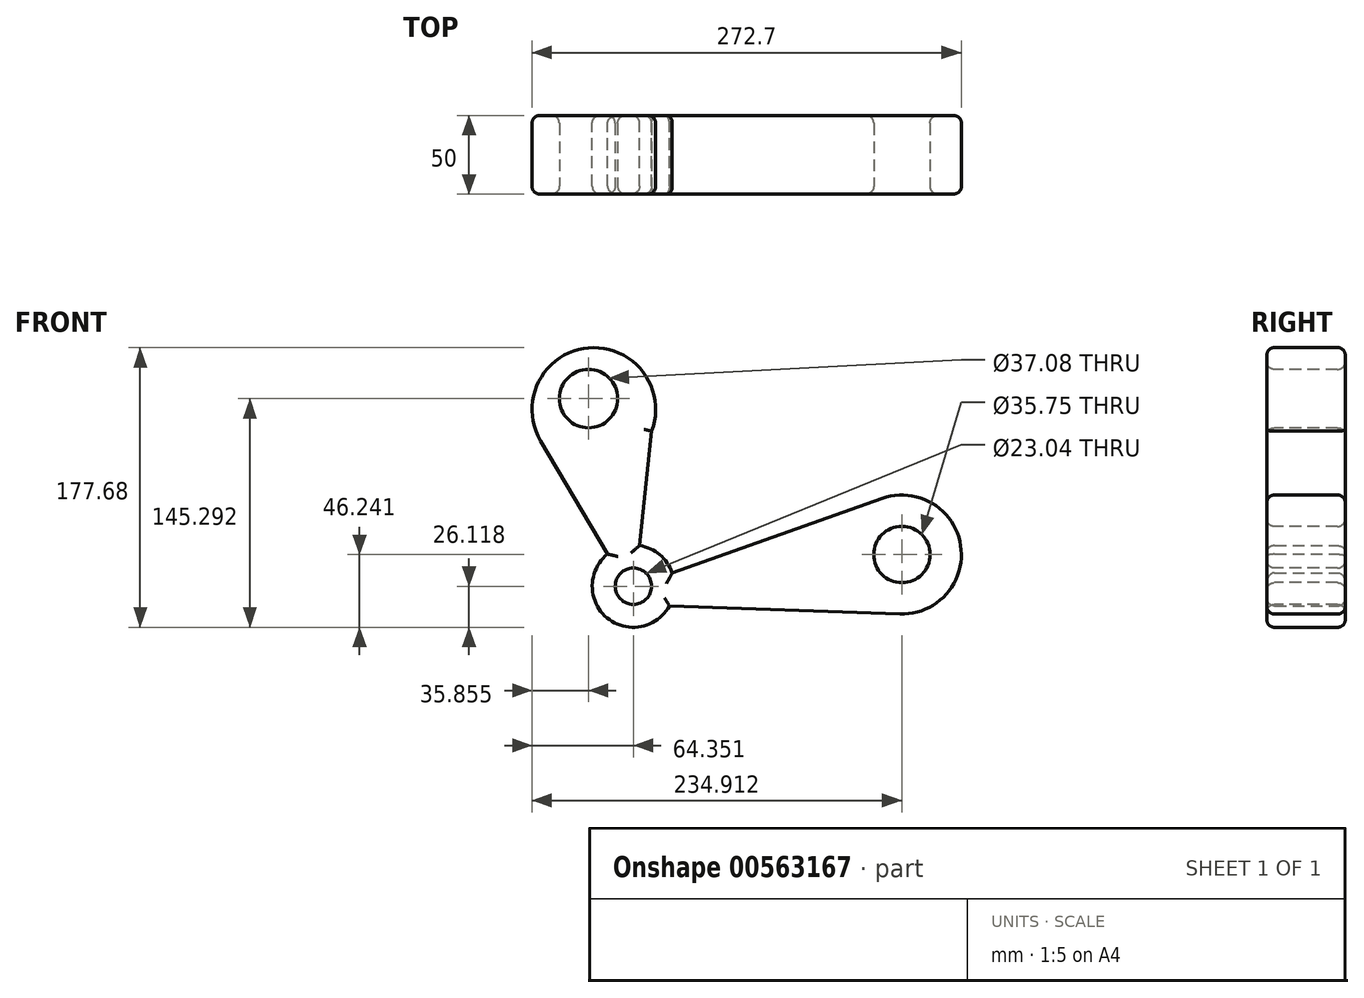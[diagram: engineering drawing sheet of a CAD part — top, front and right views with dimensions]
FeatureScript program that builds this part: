
annotation { "Feature Type Name" : "Feature", "Feature Type Description" : "" }
export const myFeature = defineFeature(function(context is Context, id is Id, definition is map)
    precondition{}
    {
        {
            var Q0;
            Q0=qCreatedBy(makeId("Front.planeOp"),FACE);
            var sketch = newSketch(context, id + "F0", { "sketchPlane" : qUnion([Q0])});
            skCircle(sketch, "E0", {"center": v(-83.68, 77.32) * mm, "radius": 39.25 * mm});
            skCircle(sketch, "E1", {"center": v(111.97, -14.86) * mm, "radius": 37.8 * mm});
            skCircle(sketch, "E2", {"center": v(-58.59, -34.98) * mm, "radius": 26.11 * mm});
            skLineSegment(sketch, "E3", {"start": v(-46.94, 63.5) * mm, "end": v(-54.54, -9.18) * mm});
            skLineSegment(sketch, "E4", {"start": v(-117.48, 57.36) * mm, "end": v(-74.96, -14.64) * mm});
            skLineSegment(sketch, "E5", {"start": v(99.34, 20.76) * mm, "end": v(-33.9, -26.48) * mm});
            skLineSegment(sketch, "E6", {"start": v(-35.66, -47.49) * mm, "end": v(110.65, -52.63) * mm});
            skSolve(sketch);
        }
        {
            var Q0;
            {var subQ0=sQuery(id+"F0.wireOp",EDGE,"E0");var subQ1=makeQuery(id+"F0.imprint","INTERSECT",VERTEX,{"derivedFrom":[subQ0,sQuery(id+"F0.wireOp",EDGE,"E3")]});Q0=makeQuery(id+"F0.imprint","IMPRINT",FACE,{"disambiguationData":[TD([[makeQuery(id+"F0.imprint","IMPRINT",EDGE,{"disambiguationData":[TD([[subQ1,1.0]])],"derivedFrom":subQ0}),1.0]])]});}
            var Q1;
            {var subQ0=sQuery(id+"F0.wireOp",EDGE,"E3");Q1=makeQuery(id+"F0.imprint","IMPRINT",FACE,{"disambiguationData":[TD([[makeQuery(id+"F0.imprint","IMPRINT",EDGE,{"derivedFrom":subQ0}),-1.0]])]});}
            var Q2;
            {var subQ0=sQuery(id+"F0.wireOp",EDGE,"E2");var subQ1=makeQuery(id+"F0.imprint","INTERSECT",VERTEX,{"derivedFrom":[subQ0,sQuery(id+"F0.wireOp",EDGE,"E3")]});Q2=makeQuery(id+"F0.imprint","IMPRINT",FACE,{"disambiguationData":[TD([[makeQuery(id+"F0.imprint","IMPRINT",EDGE,{"disambiguationData":[TD([[subQ1,1.0]])],"derivedFrom":subQ0}),1.0]])]});}
            var Q3;
            {var subQ0=sQuery(id+"F0.wireOp",EDGE,"E5");Q3=makeQuery(id+"F0.imprint","IMPRINT",FACE,{"disambiguationData":[TD([[makeQuery(id+"F0.imprint","IMPRINT",EDGE,{"derivedFrom":subQ0}),1.0]])]});}
            var Q4;
            {var subQ0=sQuery(id+"F0.wireOp",EDGE,"E1");var subQ1=makeQuery(id+"F0.imprint","INTERSECT",VERTEX,{"derivedFrom":[subQ0,sQuery(id+"F0.wireOp",EDGE,"E5")]});Q4=makeQuery(id+"F0.imprint","IMPRINT",FACE,{"disambiguationData":[TD([[makeQuery(id+"F0.imprint","IMPRINT",EDGE,{"disambiguationData":[TD([[subQ1,-1.0]])],"derivedFrom":subQ0}),1.0]])]});}
            extrude(context, id + "F1", {"entities" : qUnion([Q0, Q1, Q2, Q3, Q4]), "depth" : 50 * mm, "offsetDistance" : 25 * mm});
        }
        {
            var Q0;
            Q0=makeQuery(id+"F1.opExtrude","CAP_FACE",FACE,{"disambiguationData":[OSD([sQuery(id+"F0.wireOp",EDGE,"E0"),sQuery(id+"F0.wireOp",EDGE,"E1"),sQuery(id+"F0.wireOp",EDGE,"E2"),sQuery(id+"F0.wireOp",EDGE,"E3"),sQuery(id+"F0.wireOp",EDGE,"E4"),sQuery(id+"F0.wireOp",EDGE,"E5"),sQuery(id+"F0.wireOp",EDGE,"E6")])],"isStart":false});
            var sketch = newSketch(context, id + "F2", { "sketchPlane" : qUnion([Q0])});
            skPoint(sketch, "E7.centerSnap0", {"position": v(-87.08, 116.43) * mm});
            skPoint(sketch, "E8.centerSnap0", {"position": v(149.32, -9.1) * mm});
            skCircle(sketch, "E9", {"center": v(-87.08, 84.2) * mm, "radius": 18.54 * mm});
            skCircle(sketch, "E10", {"center": v(111.97, -14.86) * mm, "radius": 17.88 * mm});
            skCircle(sketch, "E11", {"center": v(-58.59, -34.98) * mm, "radius": 11.52 * mm});
            skSolve(sketch);
        }
        {
            var Q0;
            Q0=makeQuery(id+"F2.imprint","IMPRINT",FACE,{"disambiguationData":[TD([[makeQuery(id+"F2.imprint","IMPRINT",EDGE,{"derivedFrom":sQuery(id+"F2.wireOp",EDGE,"E10")}),1.0]])]});
            var Q1;
            Q1=makeQuery(id+"F2.imprint","IMPRINT",FACE,{"disambiguationData":[TD([[makeQuery(id+"F2.imprint","IMPRINT",EDGE,{"derivedFrom":sQuery(id+"F2.wireOp",EDGE,"E9")}),1.0]])]});
            extrude(context, id + "F3", {"entities" : qUnion([Q0, Q1]), "operationType" : NewBodyOperationType.REMOVE, "endBound" : BoundingType.THROUGH_ALL, "oppositeDirection" : true, "depth" : 25 * mm, "offsetDistance" : 25 * mm});
        }
        {
            var Q0;
            Q0 = qSketchRegion(id + "F2", true);
            extrude(context, id + "F4", {"entities" : qUnion([Q0]), "operationType" : NewBodyOperationType.REMOVE, "endBound" : BoundingType.THROUGH_ALL, "oppositeDirection" : true, "depth" : 25 * mm, "offsetDistance" : 25 * mm});
        }
        {
            var Q0;
            Q0=makeQuery(id+"F1.opExtrude","CAP_FACE",FACE,{"disambiguationData":[OSD([sQuery(id+"F0.wireOp",EDGE,"E0"),sQuery(id+"F0.wireOp",EDGE,"E1"),sQuery(id+"F0.wireOp",EDGE,"E2"),sQuery(id+"F0.wireOp",EDGE,"E3"),sQuery(id+"F0.wireOp",EDGE,"E4"),sQuery(id+"F0.wireOp",EDGE,"E5"),sQuery(id+"F0.wireOp",EDGE,"E6")])],"isStart":false});
            fillet(context, id + "F5", {"entities" : qUnion([Q0]), "radius" : 5 * mm, "tangentPropagation" : true, "allowEdgeOverflow" : false});
        }
        {
            var Q0;
            Q0=makeQuery(id+"F1.opExtrude","CAP_FACE",FACE,{"disambiguationData":[OSD([sQuery(id+"F0.wireOp",EDGE,"E0"),sQuery(id+"F0.wireOp",EDGE,"E1"),sQuery(id+"F0.wireOp",EDGE,"E2"),sQuery(id+"F0.wireOp",EDGE,"E3"),sQuery(id+"F0.wireOp",EDGE,"E4"),sQuery(id+"F0.wireOp",EDGE,"E5"),sQuery(id+"F0.wireOp",EDGE,"E6")])],"isStart":true});
            fillet(context, id + "F6", {"entities" : qUnion([Q0]), "radius" : 5 * mm, "tangentPropagation" : true, "allowEdgeOverflow" : false});
        }
    });
